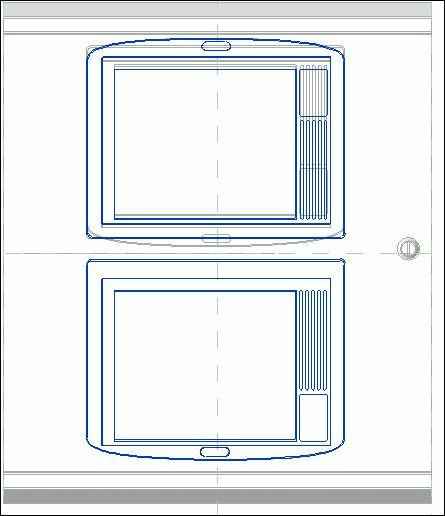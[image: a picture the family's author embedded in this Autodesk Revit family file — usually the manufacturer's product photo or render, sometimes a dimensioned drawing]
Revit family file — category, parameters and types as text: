
# Revit family: Tyco _ FPP (FireClass) _ Graphical User Interface___
name_source: partatom
category: Fire Alarm Devices
revit_build: Autodesk Revit 2016 (Build: 20150714_1515(x64)
units: mm (PartAtom-declared; Revit-internal decimal feet)

## family parameters
Always vertical = Yes
Cut with Voids When Loaded = No
Host = Wall
Maintain Annotation Orientation = No
OmniClass Number = 23.85.30.00
OmniClass Title = Safety and Security Information Systems
Part Type = Normal
Room Calculation Point = No
Round Connector Dimension = Use Diameter
Shared = No

## types (5) — shared parameters
Asset Type = Moveable
Brand = FireClass
Category = Ee_40_15_75
Colour = Anthracite Grey
Duration Unit = Year
Has Protective Earth = TRUE
IP_Code = IP30
Installation Date = 1900-12-31T23:59:59
Manufacturer = Tyco Fire & Security GmbH
Manufacturer Name = Tyco Fire & Security GmbH
Manufacturer URL = www.zettlerfire.com
ManufacturerURL = www.zettlerfire.com
Material = Plastic PC-ABS
NBS Description = Fire detection and alarm control and indicating equipment (CIE)
NBS Reference = 90-75-30/380
No Of Zonal LEDs = 16
Nominal Height = 195 mm  [stored 0.639764 ft]
Nominal Length = 33 mm  [stored 0.108268 ft]
Nominal Voltage = 18-29V DC
Nominal Width = 248 mm  [stored 0.813648 ft]
Operation Temperature Range = -5 °C to +40 °C
Product Information URL = http://www.zettlerfire.com
Relative Humidity = 95% RH continuous (non-condensing)
Shape = Rectangle
Single = Yes
Storage Temperature = -20 °C to +70 °C
URL = http://www.fireclass.net
Uniclass2 = Ee_40_15_75
Version = 1
Warranty Description = The 36 month warranty is applicable from the date of manufacture.
Warranty Duration Labor = 3
Warranty Duration Parts = 3 years
Warranty Duration Unit = Year
Warranty Start Date = 1900-12-31T23:59:59
Weight = .0.8 kg
zero-valued in all types: Expected Life, Replacement Cost

## per-type parameters (varying)
| type | Description | Model Number | Nominal Current | Product Codes | Product Description | Product Specification |
| FC1DS | FC1DS FireClass Fully Functional Repeater | Pro215S | 0.27A DC | 557.200.954 | FireClass repeater compact TFT display 16 zone DC powered with shallow Box | FireClass repeater compact TFT display 16 zone DC powered with
shallow backbox |
| FC1D2 | FC1D2 FireClass Display Only Repeater | Pro215S | 0.3A DC
0.3A DC
0.3A DC | 557.200.955 | FireClass Display Only repeater compact TFT display 16 zone DC powered with shallow backbox | FireClass Display Only repeater compact TFT display 16 zone DC powered with shallow backbox |
| FC8AS | FC8AS FireClass 80 Zone AC Repeater | Pro215S | 0.3A DC | 557.200.956 | FC8AS FireClass 80 Zone AC Repeater | FC8AS FireClass 80 Zone AC Repeater |
| FCZ4DS | FCZ4DS FireClass 40 Zone Display | Pro215S | 0.3A DC | 557.200.957 | FCZ4DS FireClass 40 Zone Display | FCZ4DS FireClass 40 Zone Display |
| FCZ8DS | FCZ8DS FireClass 80 Zone Display | FCZ8DS | 0.3A DC | 557.200.958 | FCZ8DS FireClass 80 Zone Display | FCZ8DS FireClass 80 Zone Display |

note: column(s) folded — value = type name in every type: Model, Name

note: [stored X ft] marks values corroborated as IEEE doubles in the binary element streams (Revit-internal decimal feet)

## geometry (parser evidence)
native form markers: Blend x2, Sweep x5
no freeform markers — native parametric forms only
